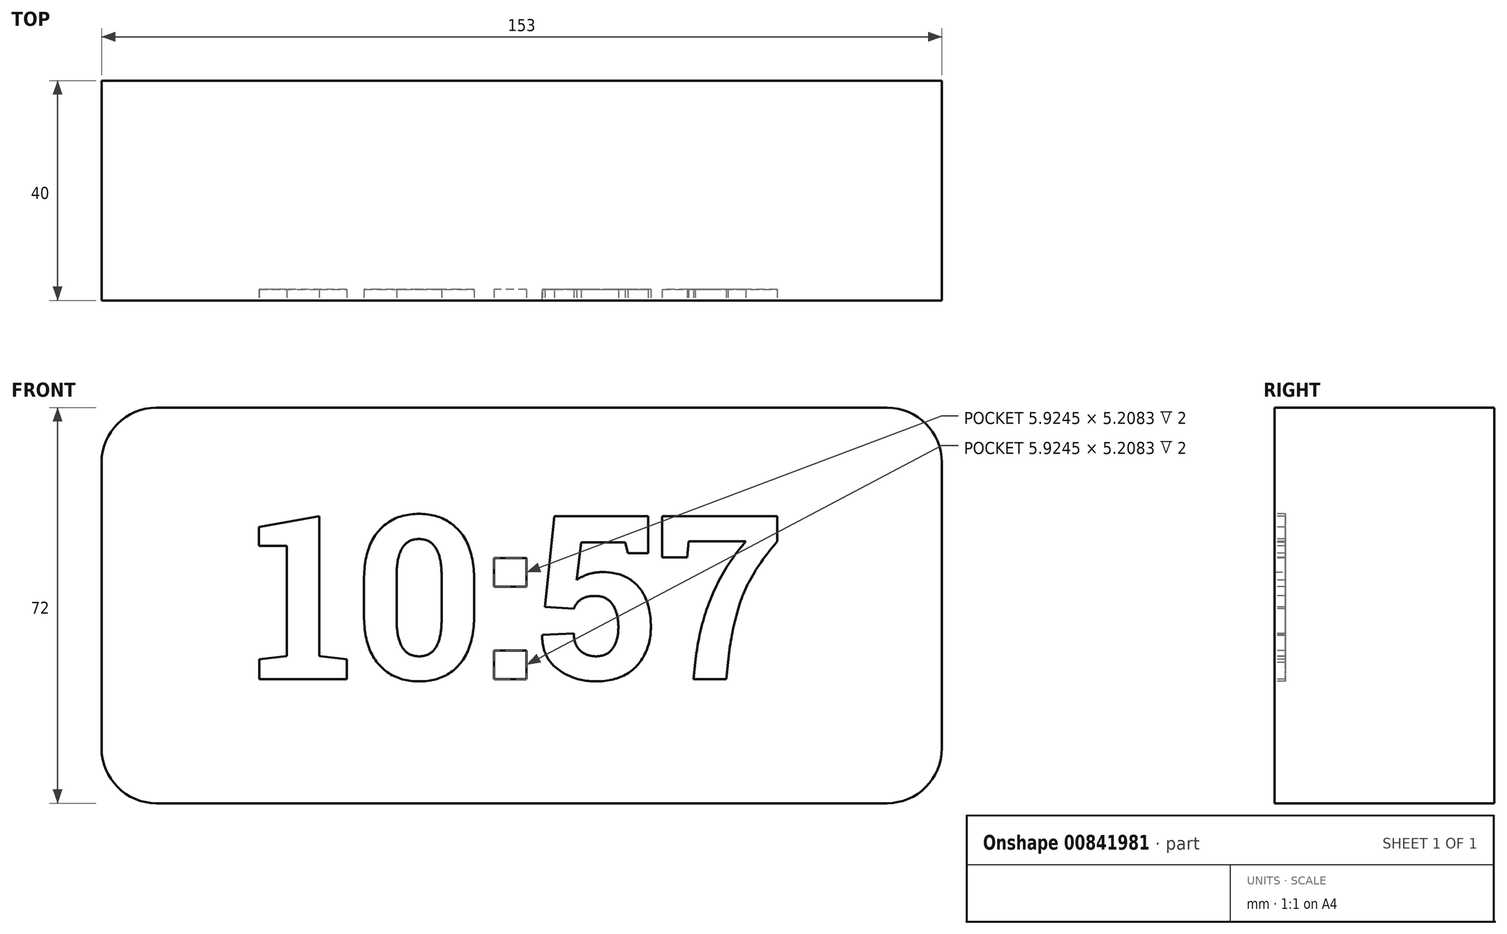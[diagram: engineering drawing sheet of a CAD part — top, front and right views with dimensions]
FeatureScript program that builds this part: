
annotation { "Feature Type Name" : "Feature", "Feature Type Description" : "" }
export const myFeature = defineFeature(function(context is Context, id is Id, definition is map)
    precondition{}
    {
        {
            var Q0;
            Q0=qCreatedBy(makeId("Front.planeOp"),FACE);
            var sketch = newSketch(context, id + "F0", { "sketchPlane" : qUnion([Q0])});
            skLineSegment(sketch, "E0.bottom", {"start": v(66.5, -36) * mm, "end": v(-66.5, -36) * mm});
            skLineSegment(sketch, "E0.top", {"start": v(66.5, 36) * mm, "end": v(-66.5, 36) * mm});
            skLineSegment(sketch, "E0.left", {"start": v(76.5, -26) * mm, "end": v(76.5, 26) * mm});
            skLineSegment(sketch, "E0.right", {"start": v(-76.5, -26) * mm, "end": v(-76.5, 26) * mm});
            skPoint(sketch, "E0.middle", {"position": v(0, 0) * mm});
            skPoint(sketch, "E1.visualSharp", {"position": v(-76.5, 36) * mm});
            skArc(sketch, "E1.filletArc", {"start": v(-66.5, 36) * mm, "mid": v(-73.57, 33.07) * mm, "end": v(-76.5, 26) * mm});
            skPoint(sketch, "E2.visualSharp", {"position": v(-76.5, -36) * mm});
            skArc(sketch, "E2.filletArc", {"start": v(-76.5, -26) * mm, "mid": v(-73.57, -33.07) * mm, "end": v(-66.5, -36) * mm});
            skPoint(sketch, "E3.visualSharp", {"position": v(76.5, -36) * mm});
            skArc(sketch, "E3.filletArc", {"start": v(66.5, -36) * mm, "mid": v(73.57, -33.07) * mm, "end": v(76.5, -26) * mm});
            skPoint(sketch, "E4.visualSharp", {"position": v(76.5, 36) * mm});
            skArc(sketch, "E4.filletArc", {"start": v(76.5, 26) * mm, "mid": v(73.57, 33.07) * mm, "end": v(66.5, 36) * mm});
            skSolve(sketch);
        }
        {
            var Q0;
            Q0 = qSketchRegion(id + "F0", true);
            extrude(context, id + "F1", {"entities" : qUnion([Q0]), "depth" : 40 * mm, "offsetDistance" : 25 * mm});
        }
        {
            var Q0;
            Q0=makeQuery(id+"F1.opExtrude","CAP_FACE",FACE,{"disambiguationData":[OSD([sQuery(id+"F0.wireOp",EDGE,"E0.bottom"),sQuery(id+"F0.wireOp",EDGE,"E0.top"),sQuery(id+"F0.wireOp",EDGE,"E0.left"),sQuery(id+"F0.wireOp",EDGE,"E0.right"),sQuery(id+"F0.wireOp",EDGE,"E1.filletArc"),sQuery(id+"F0.wireOp",EDGE,"E2.filletArc"),sQuery(id+"F0.wireOp",EDGE,"E3.filletArc"),sQuery(id+"F0.wireOp",EDGE,"E4.filletArc")])],"isStart":false});
            var sketch = newSketch(context, id + "F2", { "sketchPlane" : qUnion([Q0])});
            skText(sketch, "E5", { "text": "10:57", "fontName": "RobotoSlab-Bold.ttf"});
            const initialGuessF2  = {"E5": [-0.04909, -0.01339, 1, 0, 0.03]};
            skSetInitialGuess(sketch, initialGuessF2);
            skSolve(sketch);
        }
        {
            var Q0;
            Q0 = qSketchRegion(id + "F2", true);
            extrude(context, id + "F3", {"entities" : qUnion([Q0]), "operationType" : NewBodyOperationType.REMOVE, "oppositeDirection" : true, "depth" : 2 * mm, "offsetDistance" : 25 * mm});
        }
    });
